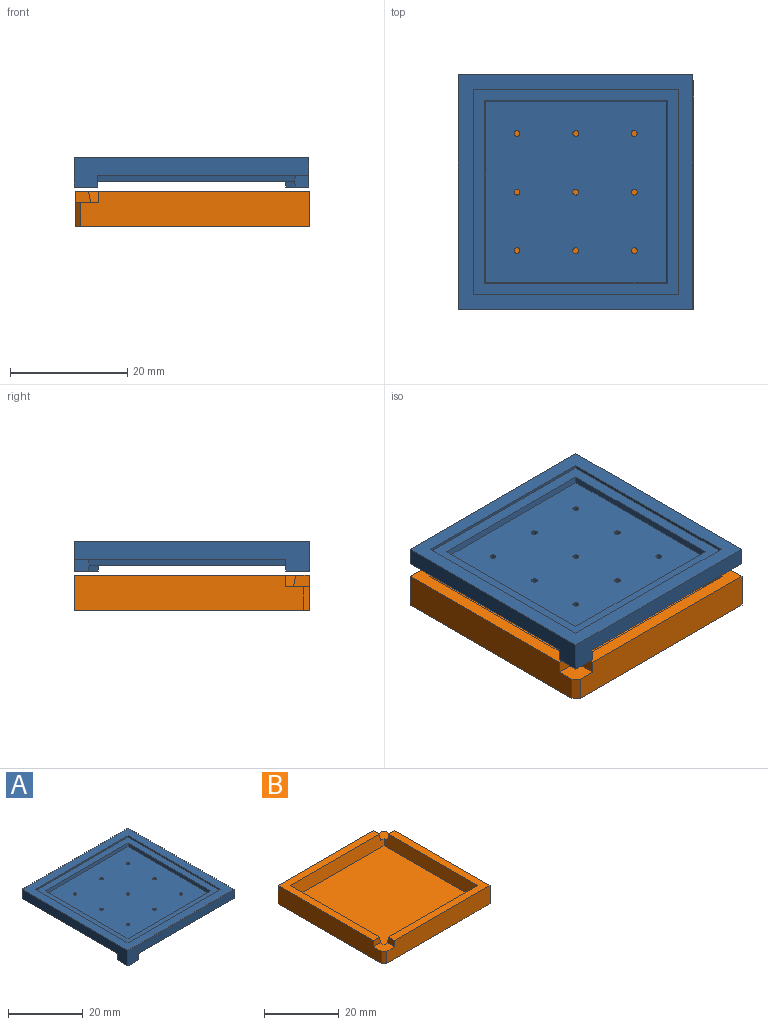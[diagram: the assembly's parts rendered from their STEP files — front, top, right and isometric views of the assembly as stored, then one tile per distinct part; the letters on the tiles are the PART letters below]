
ASSEMBLY  parts=2 mates=1
PART A: 41 faces, bbox 40x40x5 mm
  f0: plane 2.48x2mm, normal (0,-1,0), area 4.8mm2, adj f2,f8,f12,f13,f37
  f1: plane 2.48x2mm, normal (-1,0,0), area 4.8mm2, adj f2,f3,f4,f9,f38
  f2: plane 4x4mm, normal (0,0,-1), area 13.1mm2, adj f0,f1,f9,f12,f37,f38
  f3: plane 36x36mm, normal (0,0,-1), area 160.3mm2, adj f1,f4,f5,f9,f10,f34
  f4: plane 33.7x1mm, normal (0,0.98,-0.17), area 34.1mm2, adj f1,f3,f5,f6
  f5: plane 33.7x1mm, normal (-0.98,0,-0.17), area 34.1mm2, adj f3,f4,f6,f34
  f6: plane 35.05x35.05mm, normal (0,0,-1), area 1213.7mm2, adj f4,f5,f13,f14,f25,f26,f27,f28
  f7: plane 40x40mm, normal (0,0,1), area 375mm2, adj f9,f10,f11,f12,f16,f17,f18,f19
  f8: plane 36x36mm, normal (0,0,-1), area 160.3mm2, adj f0,f11,f12,f13,f14,f35
  f9: plane 40x5mm, normal (0,1,0), area 128mm2, adj f1,f2,f3,f7,f10,f12
  f10: plane 40x5mm, normal (-1,0,0), area 128mm2, adj f3,f7,f9,f11,f34,f36
  f11: plane 40x5mm, normal (0,-1,0), area 128mm2, adj f7,f8,f10,f12,f35,f36
  f12: plane 40x5mm, normal (1,0,0), area 128mm2, adj f0,f2,f7,f8,f9,f11
  f13: plane 33.7x1mm, normal (0.98,0,-0.17), area 34.1mm2, adj f0,f6,f8,f14
  f14: plane 33.7x1mm, normal (0,-0.98,-0.17), area 34.1mm2, adj f6,f8,f13,f35
  f15: plane 35x35mm, normal (0,0,1), area 251.3mm2, adj f16,f17,f18,f19,f20,f21,f22,f23
  f16: plane 35x0.5mm, normal (0,-1,0), area 17.5mm2, adj f7,f15,f17,f19
  f17: plane 35x0.5mm, normal (1,0,0), area 17.5mm2, adj f7,f15,f16,f18
  f18: plane 35x0.5mm, normal (0,1,0), area 17.5mm2, adj f7,f15,f17,f19
  f19: plane 35x0.5mm, normal (-1,0,0), area 17.5mm2, adj f7,f15,f16,f18
  f20: plane 31.2x1mm, normal (0.98,0,0.17), area 31.5mm2, adj f15,f21,f23,f24
  f21: plane 31.2x1mm, normal (0,-0.98,0.17), area 31.5mm2, adj f15,f20,f22,f24
  f22: plane 31.2x1mm, normal (-0.98,0,0.17), area 31.5mm2, adj f15,f21,f23,f24
  f23: plane 31.2x1mm, normal (0,0.98,0.17), area 31.5mm2, adj f15,f20,f22,f24
  f24: plane 30.85x30.85mm, normal (0,0,1), area 944.8mm2, adj f20,f21,f22,f23,f25,f26,f27,f28
  f25: cone r=0.5mm half-angle=5deg, axis (0,0,-1), area 9.6mm2, adj f6,f24
  f26: cone r=0.5mm half-angle=5deg, axis (0,0,-1), area 9.6mm2, adj f6,f24
  f27: cone r=0.5mm half-angle=5deg, axis (0,0,-1), area 9.6mm2, adj f6,f24
  f28: cone r=0.5mm half-angle=5deg, axis (0,0,-1), area 9.6mm2, adj f6,f24
  f29: cone r=0.5mm half-angle=5deg, axis (0,0,-1), area 9.6mm2, adj f6,f24
  f30: cone r=0.5mm half-angle=5deg, axis (0,0,-1), area 9.6mm2, adj f6,f24
  f31: cone r=0.5mm half-angle=5deg, axis (0,0,-1), area 9.6mm2, adj f6,f24
  f32: cone r=0.5mm half-angle=5deg, axis (0,0,-1), area 9.6mm2, adj f6,f24
  f33: cone r=0.5mm half-angle=5deg, axis (0,0,-1), area 9.6mm2, adj f6,f24
  f34: plane 2.48x2mm, normal (0,1,0), area 4.8mm2, adj f3,f5,f10,f36,f39
  f35: plane 2.48x2mm, normal (1,0,0), area 4.8mm2, adj f8,f11,f14,f36,f40
  f36: plane 4x4mm, normal (0,0,-1), area 13.1mm2, adj f10,f11,f34,f35,f39,f40
  f37: plane 1.7x1mm, normal (-0.98,0,-0.17), area 1.6mm2, adj f0,f2,f6,f38
  f38: plane 1.7x1mm, normal (0,-0.98,-0.17), area 1.6mm2, adj f1,f2,f6,f37
  f39: plane 1.7x1mm, normal (0.98,0,-0.17), area 1.6mm2, adj f6,f34,f36,f40
  f40: plane 1.7x1mm, normal (0,0.98,-0.17), area 1.6mm2, adj f6,f35,f36,f39
PART B: 20 faces, bbox 40x40x6 mm
  f0: plane 39x6mm, normal (0,1,0), area 228mm2, adj f1,f4,f7,f10,f18,f19
  f1: plane 39x6mm, normal (-1,0,0), area 228mm2, adj f0,f4,f8,f10,f15,f16
  f2: plane 39x6mm, normal (0,-1,0), area 228mm2, adj f3,f8,f9,f10,f14,f16
  f3: plane 36x36mm, normal (0,0,1), area 160.3mm2, adj f2,f6,f9,f12,f14,f17
  f4: plane 36x36mm, normal (0,0,1), area 160.3mm2, adj f0,f1,f5,f11,f15,f18
  f5: plane 35.05x4mm, normal (0.98,0,0.17), area 137.8mm2, adj f4,f6,f11,f13,f15,f16
  f6: plane 35.05x4mm, normal (0,0.98,0.17), area 137.8mm2, adj f3,f5,f12,f13,f14,f16
  f7: plane 4x1mm, normal (0.71,0.71,0), area 5.7mm2, adj f0,f9,f10,f19
  f8: plane 4x1mm, normal (-0.71,-0.71,0), area 5.7mm2, adj f1,f2,f10,f16
  f9: plane 39x6mm, normal (1,0,0), area 228mm2, adj f2,f3,f7,f10,f17,f19
  f10: plane 40x40mm, normal (0,0,-1), area 1599mm2, adj f0,f1,f2,f7,f8,f9
  f11: plane 35.05x4mm, normal (0,-0.98,0.17), area 137.8mm2, adj f4,f5,f12,f13,f18,f19
  f12: plane 35.05x4mm, normal (-0.98,0,0.17), area 137.8mm2, adj f3,f6,f11,f13,f17,f19
  f13: plane 33.99x33.99mm, normal (0,0,1), area 1155.3mm2, adj f5,f6,f11,f12
  f14: plane 2.65x2mm, normal (-1,0,0), area 5mm2, adj f2,f3,f6,f16
  f15: plane 2.65x2mm, normal (0,-1,0), area 5mm2, adj f1,f4,f5,f16
  f16: plane 4x4mm, normal (0,0,1), area 13.7mm2, adj f1,f2,f5,f6,f8,f14,f15
  f17: plane 2.65x2mm, normal (0,1,0), area 5mm2, adj f3,f9,f12,f19
  f18: plane 2.65x2mm, normal (1,0,0), area 5mm2, adj f0,f4,f11,f19
  f19: plane 4x4mm, normal (0,0,1), area 13.7mm2, adj f0,f7,f9,f11,f12,f17,f18
PLACE A t=(-0.1,-0.04,0.69)mm
PLACE B at identity
MATE parallel A.f13 <-> B.f12  axis (0.98,0,-0.17) through (37.51,19.15,8.19)mm
